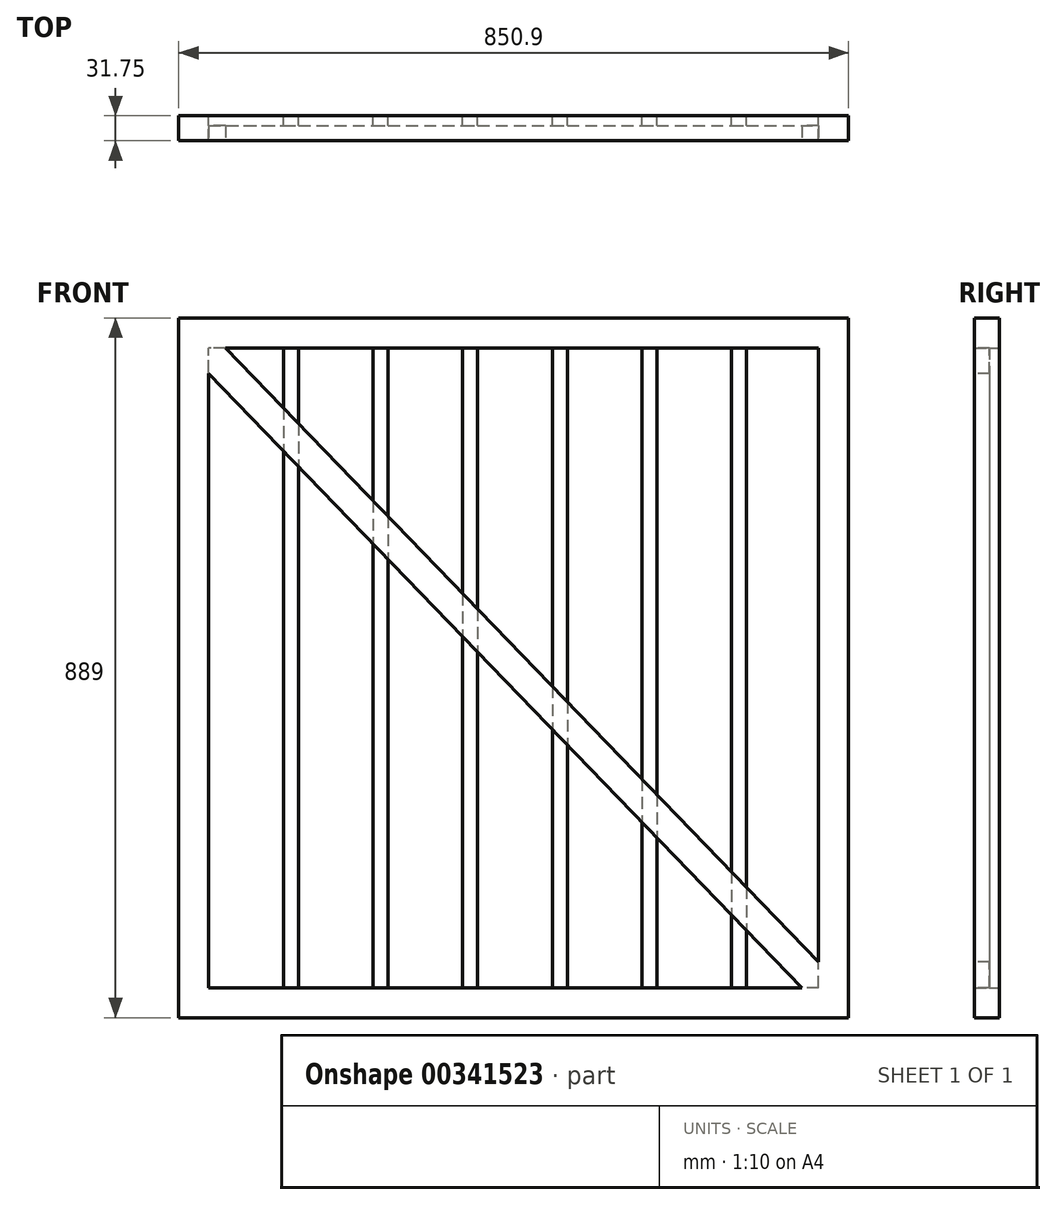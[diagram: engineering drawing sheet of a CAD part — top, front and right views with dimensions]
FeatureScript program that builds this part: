
annotation { "Feature Type Name" : "Feature", "Feature Type Description" : "" }
export const myFeature = defineFeature(function(context is Context, id is Id, definition is map)
    precondition{}
    {
        {
            var Q0;
            Q0=qCreatedBy(makeId("Front.planeOp"),FACE);
            var sketch = newSketch(context, id + "F0", { "sketchPlane" : qUnion([Q0])});
            skLineSegment(sketch, "E0.bottom", {"start": v(425.45, -444.5) * mm, "end": v(-425.45, -444.5) * mm});
            skLineSegment(sketch, "E0.top", {"start": v(425.45, 444.5) * mm, "end": v(-425.45, 444.5) * mm});
            skLineSegment(sketch, "E0.left", {"start": v(425.45, -444.5) * mm, "end": v(425.45, 444.5) * mm});
            skLineSegment(sketch, "E0.right", {"start": v(-425.45, -444.5) * mm, "end": v(-425.45, 444.5) * mm});
            skPoint(sketch, "E0.middle", {"position": v(0, 0) * mm});
            skLineSegment(sketch, "E1.bottom", {"start": v(387.35, -406.4) * mm, "end": v(-387.35, -406.4) * mm});
            skLineSegment(sketch, "E1.top", {"start": v(387.35, 406.4) * mm, "end": v(-387.35, 406.4) * mm});
            skLineSegment(sketch, "E1.left", {"start": v(387.35, -406.4) * mm, "end": v(387.35, 406.4) * mm});
            skLineSegment(sketch, "E1.right", {"start": v(-387.35, -406.4) * mm, "end": v(-387.35, 406.4) * mm});
            skSolve(sketch);
        }
        {
            var Q0;
            Q0=makeQuery(id+"F0.imprint","IMPRINT",FACE,{"disambiguationData":[TD([[makeQuery(id+"F0.imprint","IMPRINT",EDGE,{"derivedFrom":sQuery(id+"F0.wireOp",EDGE,"E0.bottom")}),-1.0]])]});
            extrude(context, id + "F1", {"entities" : qUnion([Q0]), "depth" : 31.75 * mm});
        }
        {
            var Q0;
            Q0=makeQuery(id+"F1.opExtrude","CAP_FACE",FACE,{"disambiguationData":[OSD([sQuery(id+"F0.wireOp",EDGE,"E0.bottom"),sQuery(id+"F0.wireOp",EDGE,"E0.top"),sQuery(id+"F0.wireOp",EDGE,"E0.left"),sQuery(id+"F0.wireOp",EDGE,"E0.right"),sQuery(id+"F0.wireOp",EDGE,"E1.bottom"),sQuery(id+"F0.wireOp",EDGE,"E1.top"),sQuery(id+"F0.wireOp",EDGE,"E1.left"),sQuery(id+"F0.wireOp",EDGE,"E1.right")])],"isStart":true});
            var sketch = newSketch(context, id + "F2", { "sketchPlane" : qUnion([Q0])});
            skLineSegment(sketch, "E2.0", {"start": v(-295.78, -406.4) * mm, "end": v(-276.73, -406.4) * mm});
            skLineSegment(sketch, "E3", {"start": v(-295.78, 406.4) * mm, "end": v(-295.78, -406.4) * mm});
            skLineSegment(sketch, "E4", {"start": v(-276.73, 406.4) * mm, "end": v(-276.73, -406.4) * mm});
            skPoint(sketch, "E5.orphan", {"position": v(-387.35, -406.4) * mm});
            skPoint(sketch, "E6.orphan", {"position": v(387.35, 406.4) * mm});
            skPoint(sketch, "E7.orphan", {"position": v(-387.35, 406.4) * mm});
            skPoint(sketch, "E8.orphan", {"position": v(387.35, -406.4) * mm});
            skLineSegment(sketch, "E9", {"start": v(-295.78, 406.4) * mm, "end": v(-276.73, 406.4) * mm});
            skLineSegment(sketch, "E10.1.0.0", {"start": v(-162.94, 406.4) * mm, "end": v(-162.94, -406.4) * mm});
            skLineSegment(sketch, "E10.2.0.0", {"start": v(-49.15, 406.4) * mm, "end": v(-49.15, -406.4) * mm});
            skLineSegment(sketch, "E10.3.0.0", {"start": v(64.64, 406.4) * mm, "end": v(64.64, -406.4) * mm});
            skLineSegment(sketch, "E10.4.0.0", {"start": v(178.43, 406.4) * mm, "end": v(178.43, -406.4) * mm});
            skLineSegment(sketch, "E10.5.0.0", {"start": v(292.23, 406.4) * mm, "end": v(292.23, -406.4) * mm});
            skLineSegment(sketch, "E10.direction1", {"start": v(-276.73, -406.4) * mm, "end": v(-162.94, -406.4) * mm, "construction": true});
            skLineSegment(sketch, "E11.1.0.0", {"start": v(-182, 406.4) * mm, "end": v(-182, -406.4) * mm});
            skLineSegment(sketch, "E11.2.0.0", {"start": v(-68.2, 406.4) * mm, "end": v(-68.2, -406.4) * mm});
            skLineSegment(sketch, "E11.3.0.0", {"start": v(45.6, 406.4) * mm, "end": v(45.6, -406.4) * mm});
            skLineSegment(sketch, "E11.4.0.0", {"start": v(159.38, 406.4) * mm, "end": v(159.38, -406.4) * mm});
            skLineSegment(sketch, "E11.5.0.0", {"start": v(273.18, 406.4) * mm, "end": v(273.18, -406.4) * mm});
            skLineSegment(sketch, "E11.direction1", {"start": v(-295.78, -406.4) * mm, "end": v(-182, -406.4) * mm, "construction": true});
            skLineSegment(sketch, "E12", {"start": v(-182, 406.4) * mm, "end": v(-162.94, 406.4) * mm});
            skLineSegment(sketch, "E13", {"start": v(-68.2, 406.4) * mm, "end": v(-49.15, 406.4) * mm});
            skLineSegment(sketch, "E14", {"start": v(45.6, 406.4) * mm, "end": v(64.64, 406.4) * mm});
            skLineSegment(sketch, "E15", {"start": v(159.38, 406.4) * mm, "end": v(178.43, 406.4) * mm});
            skLineSegment(sketch, "E16", {"start": v(273.18, 406.4) * mm, "end": v(292.23, 406.4) * mm});
            skLineSegment(sketch, "E17", {"start": v(-68.2, -406.4) * mm, "end": v(-49.15, -406.4) * mm});
            skLineSegment(sketch, "E18", {"start": v(-182, -406.4) * mm, "end": v(-162.94, -406.4) * mm});
            skLineSegment(sketch, "E19", {"start": v(45.6, -406.4) * mm, "end": v(64.64, -406.4) * mm});
            skLineSegment(sketch, "E20", {"start": v(159.38, -406.4) * mm, "end": v(178.43, -406.4) * mm});
            skLineSegment(sketch, "E21", {"start": v(273.18, -406.4) * mm, "end": v(292.23, -406.4) * mm});
            skSolve(sketch);
        }
        {
            var Q0;
            Q0 = qSketchRegion(id + "F2", true);
            extrude(context, id + "F3", {"entities" : qUnion([Q0]), "operationType" : NewBodyOperationType.ADD, "oppositeDirection" : true, "depth" : 12.7 * mm});
        }
        {
            var Q0;
            Q0=makeQuery(id+"F1.opExtrude","CAP_FACE",FACE,{"disambiguationData":[OSD([sQuery(id+"F0.wireOp",EDGE,"E0.bottom"),sQuery(id+"F0.wireOp",EDGE,"E0.top"),sQuery(id+"F0.wireOp",EDGE,"E0.left"),sQuery(id+"F0.wireOp",EDGE,"E0.right"),sQuery(id+"F0.wireOp",EDGE,"E1.bottom"),sQuery(id+"F0.wireOp",EDGE,"E1.top"),sQuery(id+"F0.wireOp",EDGE,"E1.left"),sQuery(id+"F0.wireOp",EDGE,"E1.right")])],"isStart":false});
            var sketch = newSketch(context, id + "F4", { "sketchPlane" : qUnion([Q0])});
            skLineSegment(sketch, "E22", {"start": v(-365.97, 406.4) * mm, "end": v(387.35, -373.69) * mm});
            skLineSegment(sketch, "E23", {"start": v(-387.35, 373.69) * mm, "end": v(365.97, -406.4) * mm});
            skLineSegment(sketch, "E24", {"start": v(-387.35, 373.69) * mm, "end": v(-387.35, 406.4) * mm});
            skLineSegment(sketch, "E25", {"start": v(-387.35, 406.4) * mm, "end": v(-365.97, 406.4) * mm});
            skLineSegment(sketch, "E26", {"start": v(387.35, -373.69) * mm, "end": v(387.35, -406.4) * mm});
            skLineSegment(sketch, "E27", {"start": v(387.35, -406.4) * mm, "end": v(365.97, -406.4) * mm});
            skSolve(sketch);
        }
        {
            var Q0;
            Q0 = qSketchRegion(id + "F4", true);
            extrude(context, id + "F5", {"entities" : qUnion([Q0]), "operationType" : NewBodyOperationType.ADD, "oppositeDirection" : true, "depth" : 19.05 * mm});
        }
    });
